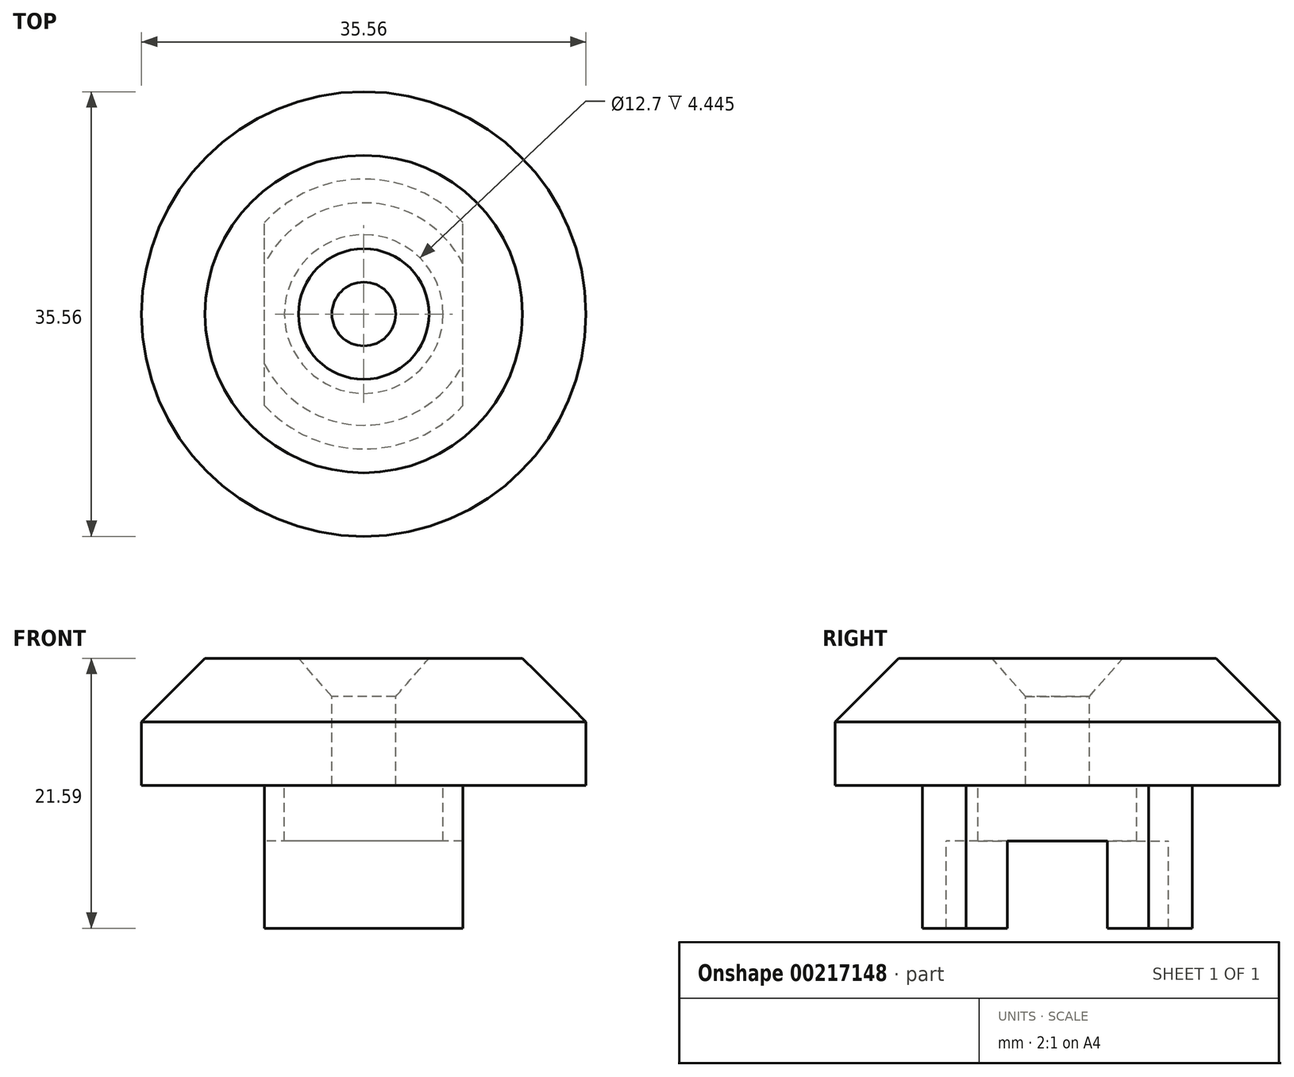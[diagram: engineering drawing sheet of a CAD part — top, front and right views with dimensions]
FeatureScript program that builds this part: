
annotation { "Feature Type Name" : "Feature", "Feature Type Description" : "" }
export const myFeature = defineFeature(function(context is Context, id is Id, definition is map)
    precondition{}
    {
        {
            var Q0;
            Q0=qCreatedBy(makeId("Top.planeOp"),FACE);
            var sketch = newSketch(context, id + "F0", { "sketchPlane" : qUnion([Q0])});
            skCircle(sketch, "E0", {"center": v(0, 0) * mm, "radius": 17.78 * mm});
            skSolve(sketch);
        }
        {
            var Q0;
            Q0 = qSketchRegion(id + "F0", true);
            extrude(context, id + "F1", {"entities" : qUnion([Q0]), "depth" : 10.16 * mm});
        }
        {
            var Q0;
            Q0=makeQuery(id+"F1.opExtrude","CAP_FACE",FACE,{"disambiguationData":[OSD([sQuery(id+"F0.wireOp",EDGE,"E0")])],"isStart":false});
            var sketch = newSketch(context, id + "F2", { "sketchPlane" : qUnion([Q0])});
            skPoint(sketch, "E1.0", {"position": v(0, 0) * mm});
            skSolve(sketch);
        }
        {
            var Q0;
            Q0=sQuery(id+"F2.wireOp",VERTEX,"E1.0");
            var Q1;
            Q1=makeQuery(id+"F1.opExtrude","SWEPT_BODY",BODY,{"disambiguationData":[OSD([sQuery(id+"F0.wireOp",EDGE,"E0")])]});
            hole(context, id + "F3", {"style" : HoleStyle.C_SINK, "endStyle" : HoleEndStyle.THROUGH, "standardTappedOrClearance" : lookupTablePath({ "standard" : "ANSI", "fit" : "Normal (ASME)", "size" : "#10", "type" : "Clearance" }), "standardBlindInLast" : lookupTablePath({ "fit" : "Free", "standard" : "ANSI", "size" : "#10", "type" : "Clearance" }), "holeDiameter" : 5.1 * mm, "cSinkDiameter" : 10.44 * mm, "cSinkAngle" : 82 * degree, "locations" : qUnion([Q0]), "scope" : qUnion([Q1]), "isTappedThrough" : true});
        }
        {
            var Q0;
            Q0=qCreatedBy(makeId("Top.planeOp"),FACE);
            var sketch = newSketch(context, id + "F4", { "sketchPlane" : qUnion([Q0])});
            skCircle(sketch, "E2", {"center": v(0, 0) * mm, "radius": 10.8 * mm});
            skLineSegment(sketch, "E3.bottom", {"start": v(7.94, -7.32) * mm, "end": v(-7.94, -7.32) * mm});
            skLineSegment(sketch, "E3.top", {"start": v(7.94, 7.32) * mm, "end": v(-7.94, 7.32) * mm});
            skLineSegment(sketch, "E3.left", {"start": v(7.94, -7.32) * mm, "end": v(7.94, 7.32) * mm});
            skLineSegment(sketch, "E3.right", {"start": v(-7.94, -7.32) * mm, "end": v(-7.94, 7.32) * mm});
            skCircle(sketch, "E4", {"center": v(0, 0) * mm, "radius": 8.9 * mm});
            skCircle(sketch, "E5", {"center": v(0, 0) * mm, "radius": 6.35 * mm});
            skSolve(sketch);
        }
        {
            var Q0;
            {var subQ0=sQuery(id+"F4.wireOp",EDGE,"E3.top");var subQ4=sQuery(id+"F4.wireOp",EDGE,"E4");var subQ5=makeQuery(id+"F4.imprint","INTERSECT",VERTEX,{"disambiguationData":[OD(0.0)],"derivedFrom":[subQ0,subQ4]});Q0=makeQuery(id+"F4.imprint","IMPRINT",FACE,{"disambiguationData":[TD([[makeQuery(id+"F4.imprint","IMPRINT",EDGE,{"disambiguationData":[TD([[subQ5,-1.0]])],"derivedFrom":subQ4}),-1.0]])]});}
            var Q1;
            {var subQ1=sQuery(id+"F4.wireOp",EDGE,"E3.top");var subQ3=sQuery(id+"F4.wireOp",EDGE,"E4");var subQ4=makeQuery(id+"F4.imprint","INTERSECT",VERTEX,{"disambiguationData":[OD(0.0)],"derivedFrom":[subQ1,subQ3]});Q1=makeQuery(id+"F4.imprint","IMPRINT",FACE,{"disambiguationData":[TD([[makeQuery(id+"F4.imprint","IMPRINT",EDGE,{"disambiguationData":[TD([[subQ4,1.0]])],"derivedFrom":subQ3}),-1.0]])]});}
            var Q2;
            {var subQ1=sQuery(id+"F4.wireOp",EDGE,"E3.top");var subQ3=sQuery(id+"F4.wireOp",EDGE,"E4");var subQ4=makeQuery(id+"F4.imprint","INTERSECT",VERTEX,{"disambiguationData":[OD(1.0)],"derivedFrom":[subQ1,subQ3]});Q2=makeQuery(id+"F4.imprint","IMPRINT",FACE,{"disambiguationData":[TD([[makeQuery(id+"F4.imprint","IMPRINT",EDGE,{"disambiguationData":[TD([[subQ4,-1.0]])],"derivedFrom":subQ3}),-1.0]])]});}
            var Q3;
            {var subQ1=sQuery(id+"F4.wireOp",EDGE,"E3.bottom");var subQ3=sQuery(id+"F4.wireOp",EDGE,"E4");var subQ4=makeQuery(id+"F4.imprint","INTERSECT",VERTEX,{"disambiguationData":[OD(1.0)],"derivedFrom":[subQ1,subQ3]});Q3=makeQuery(id+"F4.imprint","IMPRINT",FACE,{"disambiguationData":[TD([[makeQuery(id+"F4.imprint","IMPRINT",EDGE,{"disambiguationData":[TD([[subQ4,1.0]])],"derivedFrom":subQ3}),-1.0]])]});}
            var Q4;
            {var subQ0=sQuery(id+"F4.wireOp",EDGE,"E3.bottom");var subQ4=sQuery(id+"F4.wireOp",EDGE,"E4");var subQ6=makeQuery(id+"F4.imprint","INTERSECT",VERTEX,{"disambiguationData":[OD(0.0)],"derivedFrom":[subQ0,subQ4]});Q4=makeQuery(id+"F4.imprint","IMPRINT",FACE,{"disambiguationData":[TD([[makeQuery(id+"F4.imprint","IMPRINT",EDGE,{"disambiguationData":[TD([[subQ6,1.0]])],"derivedFrom":subQ4}),-1.0]])]});}
            var Q5;
            {var subQ1=sQuery(id+"F4.wireOp",EDGE,"E3.bottom");var subQ3=sQuery(id+"F4.wireOp",EDGE,"E4");var subQ4=makeQuery(id+"F4.imprint","INTERSECT",VERTEX,{"disambiguationData":[OD(0.0)],"derivedFrom":[subQ1,subQ3]});Q5=makeQuery(id+"F4.imprint","IMPRINT",FACE,{"disambiguationData":[TD([[makeQuery(id+"F4.imprint","IMPRINT",EDGE,{"disambiguationData":[TD([[subQ4,-1.0]])],"derivedFrom":subQ3}),-1.0]])]});}
            extrude(context, id + "F5", {"entities" : qUnion([Q0, Q1, Q2, Q3, Q4, Q5]), "operationType" : NewBodyOperationType.ADD, "oppositeDirection" : true, "depth" : 11.43 * mm});
        }
        {
            var Q0;
            Q0=makeQuery(id+"F4.imprint","IMPRINT",FACE,{"disambiguationData":[TD([[makeQuery(id+"F4.imprint","IMPRINT",EDGE,{"derivedFrom":sQuery(id+"F4.wireOp",EDGE,"E5")}),-1.0]])]});
            var Q1;
            {var subQ0=sQuery(id+"F4.wireOp",EDGE,"E4");var subQ1=sQuery(id+"F4.wireOp",EDGE,"E3.bottom");var subQ2=makeQuery(id+"F4.imprint","INTERSECT",VERTEX,{"disambiguationData":[OD(0.0)],"derivedFrom":[subQ1,subQ0]});Q1=makeQuery(id+"F4.imprint","IMPRINT",FACE,{"disambiguationData":[TD([[makeQuery(id+"F4.imprint","IMPRINT",EDGE,{"disambiguationData":[TD([[subQ2,-1.0]])],"derivedFrom":subQ1}),1.0]])]});}
            var Q2;
            {var subQ0=sQuery(id+"F4.wireOp",EDGE,"E4");var subQ1=sQuery(id+"F4.wireOp",EDGE,"E3.top");var subQ2=makeQuery(id+"F4.imprint","INTERSECT",VERTEX,{"disambiguationData":[OD(0.0)],"derivedFrom":[subQ1,subQ0]});Q2=makeQuery(id+"F4.imprint","IMPRINT",FACE,{"disambiguationData":[TD([[makeQuery(id+"F4.imprint","IMPRINT",EDGE,{"disambiguationData":[TD([[subQ2,-1.0]])],"derivedFrom":subQ1}),-1.0]])]});}
            extrude(context, id + "F6", {"entities" : qUnion([Q0, Q1, Q2]), "operationType" : NewBodyOperationType.ADD, "oppositeDirection" : true, "depth" : 4.44 * mm});
        }
        {
            var Q0;
            Q0=makeQuery(id+"F1.opExtrude","CAP_EDGE",EDGE,{"disambiguationData":[OSD([sQuery(id+"F0.wireOp",EDGE,"E0")])],"isStart":false});
            chamfer(context, id + "F7", {"entities" : qUnion([Q0]), "width" : 5.08 * mm, "tangentPropagation" : true});
        }
    });
